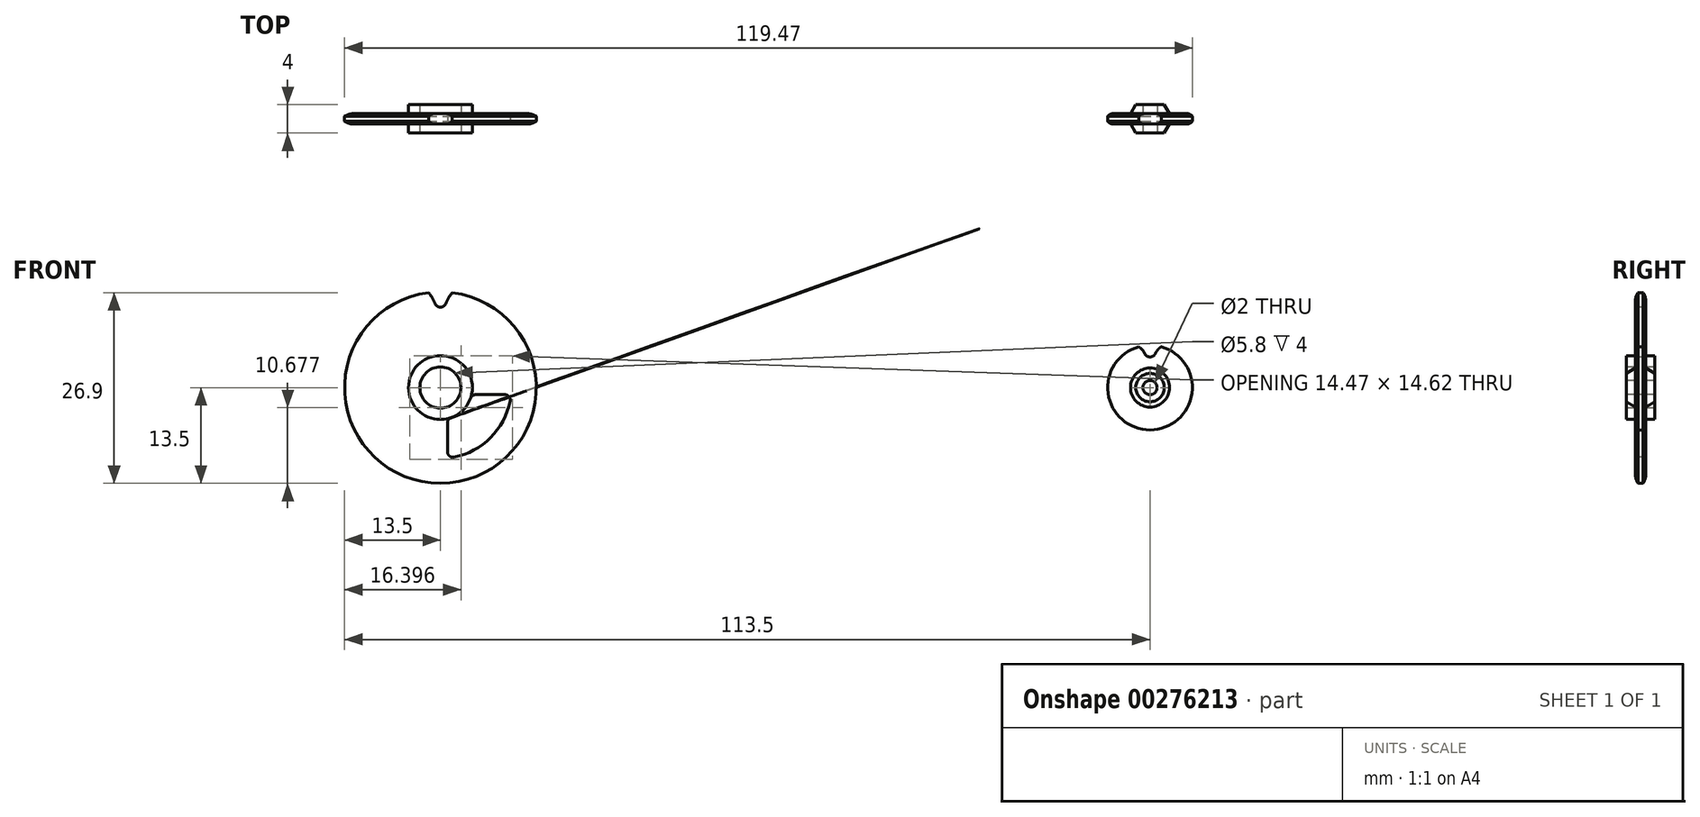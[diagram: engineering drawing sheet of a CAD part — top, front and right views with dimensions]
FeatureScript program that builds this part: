
annotation { "Feature Type Name" : "Feature", "Feature Type Description" : "" }
export const myFeature = defineFeature(function(context is Context, id is Id, definition is map)
    precondition{}
    {
        {
            var Q0;
            Q0=qCreatedBy(makeId("Front.planeOp"),FACE);
            var sketch = newSketch(context, id + "F0", { "sketchPlane" : qUnion([Q0])});
            skCircle(sketch, "E0", {"center": v(0, 0) * mm, "radius": 5.14 * mm, "construction": true});
            skLineSegment(sketch, "E1", {"start": v(-1.59, 4.89) * mm, "end": v(1.59, 4.89) * mm, "construction": true});
            skLineSegment(sketch, "E2", {"start": v(0, 0) * mm, "end": v(-1.59, 4.89) * mm, "construction": true});
            skLineSegment(sketch, "E3", {"start": v(0, 0) * mm, "end": v(1.59, 4.89) * mm, "construction": true});
            skArc(sketch, "E4", {"start": v(-0.75, 4.8) * mm, "mid": v(0, 4.31) * mm, "end": v(0.75, 4.8) * mm});
            skLineSegment(sketch, "E5", {"start": v(0, 5.14) * mm, "end": v(-1.45, 4.47) * mm, "construction": true});
            skLineSegment(sketch, "E6", {"start": v(0, 5.14) * mm, "end": v(1.45, 4.47) * mm, "construction": true});
            skCircle(sketch, "E7", {"center": v(0, 0) * mm, "radius": 6.47 * mm, "construction": true});
            skArc(sketch, "E8", {"start": v(-0.75, 4.8) * mm, "mid": v(-1.38, 5.6) * mm, "end": v(-2.3, 6.05) * mm});
            skArc(sketch, "E9", {"start": v(0.75, 4.8) * mm, "mid": v(1.38, 5.6) * mm, "end": v(2.3, 6.05) * mm});
            skCircle(sketch, "E10", {"center": v(0, 5.14) * mm, "radius": 0.82 * mm, "construction": true});
            skArc(sketch, "E11", {"start": v(2.3, 6.05) * mm, "mid": v(0, 6.47) * mm, "end": v(-2.3, 6.05) * mm});
            skSolve(sketch);
        }
        {
            var Q0;
            Q0=qCreatedBy(makeId("Right.planeOp"),FACE);
            var sketch = newSketch(context, id + "F1", { "sketchPlane" : qUnion([Q0])});
            skLineSegment(sketch, "E12", {"start": v(-3.5, 0) * mm, "end": v(5.06, 0) * mm, "construction": true});
            skLineSegment(sketch, "E13", {"start": v(0, 1) * mm, "end": v(2, 1) * mm});
            skLineSegment(sketch, "E14", {"start": v(2, 1) * mm, "end": v(2, 2) * mm});
            skLineSegment(sketch, "E15", {"start": v(2, 2) * mm, "end": v(0.74, 2.75) * mm});
            skLineSegment(sketch, "E16", {"start": v(0.74, 2.75) * mm, "end": v(0.74, 5.14) * mm});
            skLineSegment(sketch, "E17", {"start": v(-2.42, 5.14) * mm, "end": v(2.3, 5.14) * mm, "construction": true});
            skArc(sketch, "E18", {"start": v(0.74, 5.14) * mm, "mid": v(0.65, 5.6) * mm, "end": v(0.36, 5.97) * mm});
            skLineSegment(sketch, "E19", {"start": v(0.36, 5.97) * mm, "end": v(0, 5.97) * mm});
            skLineSegment(sketch, "E20.MirrorCS", {"start": v(-0.36, 5.97) * mm, "end": v(0, 5.97) * mm});
            skArc(sketch, "E21.MirrorCS", {"start": v(-0.74, 5.14) * mm, "mid": v(-0.65, 5.6) * mm, "end": v(-0.36, 5.97) * mm});
            skLineSegment(sketch, "E22.MirrorCS", {"start": v(-2, 1) * mm, "end": v(-2, 2) * mm});
            skLineSegment(sketch, "E23.MirrorCS", {"start": v(0, 1) * mm, "end": v(-2, 1) * mm});
            skLineSegment(sketch, "E24.MirrorCS", {"start": v(-2, 2) * mm, "end": v(-0.74, 2.75) * mm});
            skLineSegment(sketch, "E25.MirrorCS", {"start": v(-0.74, 2.75) * mm, "end": v(-0.74, 5.14) * mm});
            skPoint(sketch, "E26", {"position": v(0, 6.47) * mm});
            skSolve(sketch);
        }
        {
            var Q0;
            Q0=makeQuery(id+"F1.imprint","IMPRINT",FACE,{"disambiguationData":[TD([[makeQuery(id+"F1.imprint","IMPRINT",EDGE,{"derivedFrom":sQuery(id+"F1.wireOp",EDGE,"E13")}),1.0]])]});
            var Q1;
            Q1=sQuery(id+"F1.wireOp",EDGE,"E12");
            revolve(context, id + "F2", {"entities" : qUnion([Q0]), "axis" : qUnion([Q1]), "revolveType" : RevolveType.FULL});
        }
        {
            var Q0;
            Q0=makeQuery(id+"F0.imprint","IMPRINT",FACE,{"disambiguationData":[TD([[makeQuery(id+"F0.imprint","IMPRINT",EDGE,{"derivedFrom":sQuery(id+"F0.wireOp",EDGE,"E4")}),1.0]])]});
            extrude(context, id + "F3", {"entities" : qUnion([Q0]), "operationType" : NewBodyOperationType.REMOVE, "endBound" : BoundingType.THROUGH_ALL, "oppositeDirection" : true, "depth" : 25 * mm, "hasSecondDirection" : true, "secondDirectionBound" : BoundingType.THROUGH_ALL, "secondDirectionOppositeDirection" : false, "secondDirectionDepth" : 25 * mm});
        }
        {
            var Q0;
            Q0=qCreatedBy(makeId("Front.planeOp"),FACE);
            var sketch = newSketch(context, id + "F4", { "sketchPlane" : qUnion([Q0])});
            skCircle(sketch, "E27", {"center": v(-100, 0) * mm, "radius": 12.16 * mm, "construction": true});
            skLineSegment(sketch, "E28", {"start": v(-101.59, 12.06) * mm, "end": v(-98.41, 12.06) * mm, "construction": true});
            skLineSegment(sketch, "E29", {"start": v(-100, 0) * mm, "end": v(-101.59, 12.06) * mm, "construction": true});
            skLineSegment(sketch, "E30", {"start": v(-100, 0) * mm, "end": v(-98.41, 12.06) * mm, "construction": true});
            skArc(sketch, "E31", {"start": v(-100.77, 11.85) * mm, "mid": v(-100, 11.34) * mm, "end": v(-99.23, 11.85) * mm});
            skLineSegment(sketch, "E32", {"start": v(-100, 12.16) * mm, "end": v(-101.52, 11.55) * mm, "construction": true});
            skLineSegment(sketch, "E33", {"start": v(-100, 12.16) * mm, "end": v(-98.48, 11.55) * mm, "construction": true});
            skCircle(sketch, "E34", {"center": v(-100, 0) * mm, "radius": 13.64 * mm, "construction": true});
            skArc(sketch, "E35", {"start": v(-100.77, 11.85) * mm, "mid": v(-101.2, 12.73) * mm, "end": v(-101.78, 13.53) * mm});
            skArc(sketch, "E36", {"start": v(-99.23, 11.85) * mm, "mid": v(-98.8, 12.73) * mm, "end": v(-98.22, 13.53) * mm});
            skCircle(sketch, "E37", {"center": v(-100, 12.16) * mm, "radius": 0.82 * mm, "construction": true});
            skArc(sketch, "E38", {"start": v(-98.22, 13.53) * mm, "mid": v(-100, 13.64) * mm, "end": v(-101.78, 13.53) * mm});
            skLineSegment(sketch, "E39", {"start": v(-100, 0) * mm, "end": v(-100, 14.43) * mm, "construction": true});
            skPoint(sketch, "E40", {"position": v(-100, 12.06) * mm});
            skSolve(sketch);
        }
        {
            var Q0;
            Q0=sQuery(id+"F4.wireOp",VERTEX,"E30.start");
            var Q1;
            Q1=qCreatedBy(makeId("Right.planeOp"),FACE);
            cPlane(context, id + "F5", {"entities" : qUnion([Q0, Q1]), "cplaneType" : CPlaneType.PLANE_POINT, "offset" : 25 * mm, "width" : 150 * mm, "height" : 150 * mm});
        }
        {
            var Q0;
            Q0=qCreatedBy(id+"F5.planeOp",FACE);
            var sketch = newSketch(context, id + "F6", { "sketchPlane" : qUnion([Q0])});
            skLineSegment(sketch, "E41", {"start": v(-5.1, 12.16) * mm, "end": v(5.4, 12.16) * mm, "construction": true});
            skLineSegment(sketch, "E42", {"start": v(-13.62, 0) * mm, "end": v(16.4, 0) * mm, "construction": true});
            skLineSegment(sketch, "E43", {"start": v(0, 2.9) * mm, "end": v(2, 2.9) * mm});
            skLineSegment(sketch, "E44", {"start": v(2, 2.9) * mm, "end": v(2, 4.5) * mm});
            skLineSegment(sketch, "E45", {"start": v(2, 4.5) * mm, "end": v(0.75, 4.5) * mm});
            skLineSegment(sketch, "E46", {"start": v(0.75, 4.5) * mm, "end": v(0.74, 12.16) * mm});
            skArc(sketch, "E47", {"start": v(0.74, 12.16) * mm, "mid": v(0.65, 12.86) * mm, "end": v(0.36, 13.5) * mm});
            skLineSegment(sketch, "E48", {"start": v(0.36, 13.5) * mm, "end": v(0, 13.5) * mm});
            skLineSegment(sketch, "E49.MirrorCS", {"start": v(-0.36, 13.5) * mm, "end": v(0, 13.5) * mm});
            skLineSegment(sketch, "E50.MirrorCS", {"start": v(0, 2.9) * mm, "end": v(-2, 2.9) * mm});
            skArc(sketch, "E51.MirrorCS", {"start": v(-0.74, 12.16) * mm, "mid": v(-0.65, 12.86) * mm, "end": v(-0.36, 13.5) * mm});
            skLineSegment(sketch, "E52.MirrorCS", {"start": v(-2, 4.5) * mm, "end": v(-0.75, 4.5) * mm});
            skLineSegment(sketch, "E53.MirrorCS", {"start": v(-2, 2.9) * mm, "end": v(-2, 4.5) * mm});
            skLineSegment(sketch, "E54.MirrorCS", {"start": v(-0.75, 4.5) * mm, "end": v(-0.74, 12.16) * mm});
            skSolve(sketch);
        }
        {
            var Q0;
            Q0=makeQuery(id+"F6.imprint","IMPRINT",FACE,{"disambiguationData":[TD([[makeQuery(id+"F6.imprint","IMPRINT",EDGE,{"derivedFrom":sQuery(id+"F6.wireOp",EDGE,"E43")}),1.0]])]});
            var Q1;
            Q1=sQuery(id+"F6.wireOp",EDGE,"E42");
            revolve(context, id + "F7", {"entities" : qUnion([Q0]), "axis" : qUnion([Q1]), "revolveType" : RevolveType.FULL});
        }
        {
            var Q0;
            Q0 = qSketchRegion(id + "F4", true);
            extrude(context, id + "F8", {"entities" : qUnion([Q0]), "operationType" : NewBodyOperationType.REMOVE, "endBound" : BoundingType.THROUGH_ALL, "oppositeDirection" : true, "depth" : 25 * mm, "hasSecondDirection" : true, "secondDirectionBound" : BoundingType.THROUGH_ALL, "secondDirectionOppositeDirection" : false, "secondDirectionDepth" : 25 * mm});
        }
        {
            var Q0;
            Q0=qCreatedBy(makeId("Front.planeOp"),FACE);
            var sketch = newSketch(context, id + "F9", { "sketchPlane" : qUnion([Q0])});
            skLineSegment(sketch, "E55", {"start": v(-83.68, 0) * mm, "end": v(-114.58, 0) * mm, "construction": true});
            skLineSegment(sketch, "E56", {"start": v(-100, -15.83) * mm, "end": v(-100, 16.2) * mm, "construction": true});
            skArc(sketch, "E57.0", {"start": v(-98.5, -4.24) * mm, "mid": v(-96.82, -3.18) * mm, "end": v(-95.76, -1.5) * mm});
            skArc(sketch, "E58", {"start": v(-90.18, -1.9) * mm, "mid": v(-92.93, -7.07) * mm, "end": v(-98.1, -9.82) * mm});
            skLineSegment(sketch, "E59", {"start": v(-99, -9.08) * mm, "end": v(-99, -4.95) * mm});
            skLineSegment(sketch, "E60", {"start": v(-90.92, -1) * mm, "end": v(-95.05, -1) * mm});
            skPoint(sketch, "E61.visualSharp", {"position": v(-99, -9.95) * mm});
            skArc(sketch, "E61.filletArc", {"start": v(-99, -9.08) * mm, "mid": v(-98.73, -9.66) * mm, "end": v(-98.1, -9.82) * mm});
            skPoint(sketch, "E62.visualSharp", {"position": v(-90.05, -1) * mm});
            skArc(sketch, "E62.filletArc", {"start": v(-90.18, -1.9) * mm, "mid": v(-90.34, -1.27) * mm, "end": v(-90.92, -1) * mm});
            skPoint(sketch, "E63.visualSharp", {"position": v(-95.61, -1) * mm});
            skArc(sketch, "E63.filletArc", {"start": v(-95.05, -1) * mm, "mid": v(-95.48, -1.14) * mm, "end": v(-95.76, -1.5) * mm});
            skPoint(sketch, "E64.visualSharp", {"position": v(-99, -4.39) * mm});
            skArc(sketch, "E64.filletArc", {"start": v(-98.5, -4.24) * mm, "mid": v(-98.86, -4.52) * mm, "end": v(-99, -4.95) * mm});
            skSolve(sketch);
        }
        {
            var Q0;
            Q0 = qSketchRegion(id + "F9", true);
            extrude(context, id + "F10", {"entities" : qUnion([Q0]), "operationType" : NewBodyOperationType.REMOVE, "endBound" : BoundingType.THROUGH_ALL, "oppositeDirection" : true, "depth" : 25 * mm, "hasSecondDirection" : true, "secondDirectionBound" : BoundingType.THROUGH_ALL, "secondDirectionOppositeDirection" : false, "secondDirectionDepth" : 25 * mm});
        }
        {
            var Q0;
            Q0=makeQuery(id+"F10.boolean.opBoolean","INTERSECT",EDGE,{"derivedFrom":[makeQuery(id+"F7.opRevolve","SWEPT_FACE",FACE,{"disambiguationData":[OSD([sQuery(id+"F6.wireOp",EDGE,"E54.MirrorCS")])]}),makeQuery(id+"F10.opExtrude","SWEPT_FACE",FACE,{"disambiguationData":[OSD([sQuery(id+"F9.wireOp",EDGE,"E58")])]})]});
            var Q1;
            Q1=makeQuery(id+"F10.boolean.opBoolean","INTERSECT",EDGE,{"derivedFrom":[makeQuery(id+"F7.opRevolve","SWEPT_FACE",FACE,{"disambiguationData":[OSD([sQuery(id+"F6.wireOp",EDGE,"E46")])]}),makeQuery(id+"F10.opExtrude","SWEPT_FACE",FACE,{"disambiguationData":[OSD([sQuery(id+"F9.wireOp",EDGE,"E59")])]})]});
            fillet(context, id + "F11", {"entities" : qUnion([Q0, Q1]), "radius" : .3 * mm, "tangentPropagation" : true, "allowEdgeOverflow" : false});
        }
    });
